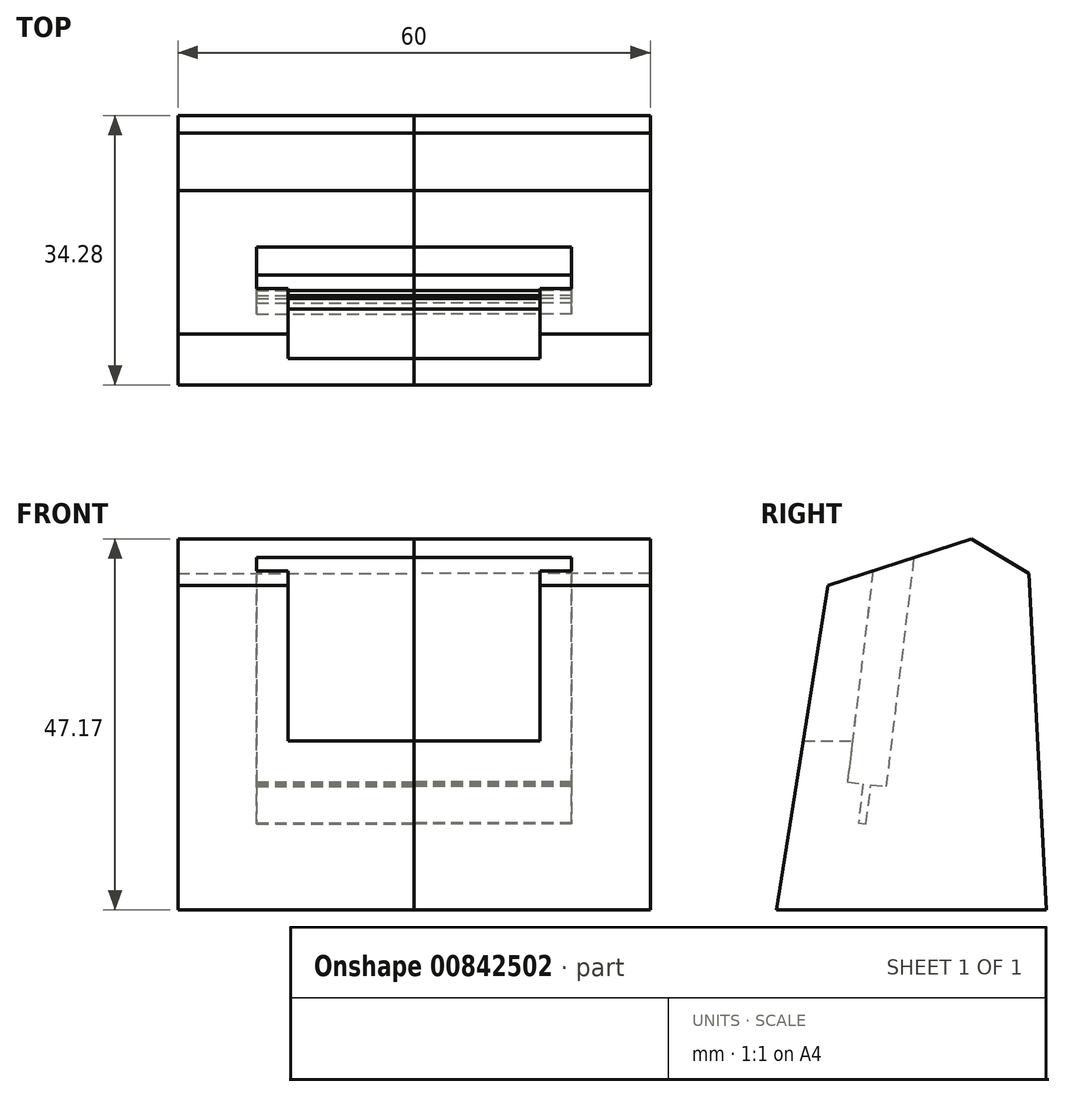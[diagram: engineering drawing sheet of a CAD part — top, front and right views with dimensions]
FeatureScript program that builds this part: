
annotation { "Feature Type Name" : "Feature", "Feature Type Description" : "" }
export const myFeature = defineFeature(function(context is Context, id is Id, definition is map)
    precondition{}
    {
        {
            var Q0;
            Q0=qCreatedBy(makeId("Right.planeOp"),FACE);
            var sketch = newSketch(context, id + "F0", { "sketchPlane" : qUnion([Q0])});
            skLineSegment(sketch, "E0", {"start": v(7.9, 0) * mm, "end": v(-17.53, 0) * mm});
            skLineSegment(sketch, "E1", {"start": v(-17.53, 0) * mm, "end": v(-11, 41.21) * mm});
            skLineSegment(sketch, "E2", {"start": v(-11, 41.21) * mm, "end": v(7.23, 47.17) * mm});
            skLineSegment(sketch, "E3", {"start": v(7.23, 47.17) * mm, "end": v(14.52, 42.75) * mm});
            skLineSegment(sketch, "E4", {"start": v(14.52, 42.75) * mm, "end": v(16.75, 0) * mm});
            skLineSegment(sketch, "E5", {"start": v(16.75, 0) * mm, "end": v(7.9, 0) * mm});
            skSolve(sketch);
        }
        {
            var Q0;
            Q0=makeQuery(id+"F0.imprint","IMPRINT",FACE,{"disambiguationData":[TD([[makeQuery(id+"F0.imprint","IMPRINT",EDGE,{"derivedFrom":sQuery(id+"F0.wireOp",EDGE,"E0")}),-1.0]])]});
            extrude(context, id + "F1", {"entities" : qUnion([Q0]), "oppositeDirection" : true, "depth" : 30 * mm, "offsetDistance" : 25 * mm});
        }
        {
            var Q0;
            Q0=makeQuery(id+"F1.opExtrude","CAP_FACE",FACE,{"disambiguationData":[OSD([sQuery(id+"F0.wireOp",EDGE,"E0"),sQuery(id+"F0.wireOp",EDGE,"E1"),sQuery(id+"F0.wireOp",EDGE,"E2"),sQuery(id+"F0.wireOp",EDGE,"unMjoF4u-tc3M-aFty-6QDb-tsXtRbBupsvK")])],"isStart":true});
            var sketch = newSketch(context, id + "F2", { "sketchPlane" : qUnion([Q0])});
            skLineSegment(sketch, "E6", {"start": v(-5.24, 43.1) * mm, "end": v(-8.5, 16.29) * mm});
            skLineSegment(sketch, "E7", {"start": v(-3.53, 15.69) * mm, "end": v(0, 44.8) * mm});
            skLineSegment(sketch, "E8", {"start": v(-6.5, 16.05) * mm, "end": v(-7.1, 11.08) * mm});
            skLineSegment(sketch, "E9", {"start": v(-7.1, 11.08) * mm, "end": v(-6.12, 10.96) * mm});
            skLineSegment(sketch, "E10", {"start": v(-6.12, 10.96) * mm, "end": v(-5.51, 15.93) * mm});
            skLineSegment(sketch, "E11", {"start": v(-8.5, 16.29) * mm, "end": v(-6.5, 16.05) * mm});
            skLineSegment(sketch, "E12", {"start": v(-5.51, 15.93) * mm, "end": v(-3.53, 15.69) * mm});
            skSolve(sketch);
        }
        {
            var Q0;
            Q0=makeQuery(id+"F2.imprint","IMPRINT",FACE,{"disambiguationData":[TD([[makeQuery(id+"F2.imprint","IMPRINT",EDGE,{"derivedFrom":sQuery(id+"F2.wireOp",EDGE,"E6")}),1.0]])]});
            var Q1;
            {var subQ0=sQuery(id+"F2.wireOp",EDGE,"E8");Q1=makeQuery(id+"F2.imprint","IMPRINT",FACE,{"disambiguationData":[TD([[makeQuery(id+"F2.imprint","IMPRINT",EDGE,{"derivedFrom":subQ0}),1.0]])]});}
            extrude(context, id + "F3", {"entities" : qUnion([Q0, Q1]), "operationType" : NewBodyOperationType.REMOVE, "oppositeDirection" : true, "depth" : 20 * mm, "offsetDistance" : 25 * mm});
        }
        {
            var Q0;
            Q0=makeQuery(id+"F1.opExtrude","CAP_FACE",FACE,{"disambiguationData":[OSD([sQuery(id+"F0.wireOp",EDGE,"E0"),sQuery(id+"F0.wireOp",EDGE,"E1"),sQuery(id+"F0.wireOp",EDGE,"E2"),sQuery(id+"F0.wireOp",EDGE,"unMjoF4u-tc3M-aFty-6QDb-tsXtRbBupsvK")])],"isStart":true});
            var sketch = newSketch(context, id + "F4", { "sketchPlane" : qUnion([Q0])});
            skLineSegment(sketch, "E13", {"start": v(-14.13, 21.46) * mm, "end": v(-7.87, 21.46) * mm});
            skLineSegment(sketch, "E14", {"start": v(-14.13, 21.46) * mm, "end": v(-11, 41.21) * mm});
            skSolve(sketch);
        }
        {
            var Q0;
            {var subQ0=sQuery(id+"F4.wireOp",EDGE,"E13");Q0=makeQuery(id+"F4.imprint","IMPRINT",FACE,{"disambiguationData":[TD([[makeQuery(id+"F4.imprint","IMPRINT",EDGE,{"derivedFrom":subQ0}),1.0]])]});}
            extrude(context, id + "F5", {"entities" : qUnion([Q0]), "operationType" : NewBodyOperationType.REMOVE, "oppositeDirection" : true, "depth" : 16 * mm, "offsetDistance" : 25 * mm});
        }
        {
            var Q0;
            Q0=makeQuery(id+"F1.opExtrude","SWEPT_BODY",BODY,{"disambiguationData":[OSD([sQuery(id+"F0.wireOp",EDGE,"E0"),sQuery(id+"F0.wireOp",EDGE,"E1"),sQuery(id+"F0.wireOp",EDGE,"E2"),sQuery(id+"F0.wireOp",EDGE,"E3"),sQuery(id+"F0.wireOp",EDGE,"E4"),sQuery(id+"F0.wireOp",EDGE,"E5")])]});
            var Q1;
            Q1=qCreatedBy(makeId("Right.planeOp"),FACE);
            mirror(context, id + "F6", {"entities" : qUnion([Q0]), "mirrorPlane" : qUnion([Q1])});
        }
    });
